# Revit family: P710076-031
name_source: partatom
category: Lighting Fixtures
revit_build: Autodesk Revit 2014 (Build: 20130308_1515(x64)
units: mm (PartAtom-declared; Revit-internal decimal feet)

## types (1)
- P710076-031
    Apparent Load = 60 VA
    Assembly Code = D5020200
    Color Filter = 16777215
    Connector Description = Lighting Connector
    Default Elevation = 48 "
    Description = Experience the sense of shelter, warmth, and protection offered by the mountain modern glow of this wall sconce. Let wandering eyes hungry for a satisfying lighting experience satiate their appetites as their gaze feasts upon the artistic yet playful tic-tac-toe pattern intricately weaved into the matte black frame. A signature seeded glass pane fosters a gazing window design that grants the light fixture a rustic, modern cabin vibe.
    Dimming Lamp Color Temperature Shift = <None>
    Fabric = Paint - Hubbell - White Texture
    Features = A signature seeded glass pane fosters a gazing window design that grants the light fixture a rustic, modern cabin vibe.
Let wandering eyes hungry for a satisfying lighting experience satiate their appetites as their gaze feasts upon the artistic yet playful tic-tac-toe pattern intricately weaved into the matte black frame.
Experience the sense of shelter, warmth, and protection offered by the mountain modern glow of this wall sconce.
Ideal for any foyer, dining room, or kitchen.
Measures 5-1/8-inch width by 14-5/8-inch height.
Uses one candelabra base bulb that is sold separately (60w max - LED or incandescent).
Able to be fully dimmable with dimmable bulbs.
Includes installation instructions and mounting hardware.
Progress Lighting products are designed for exceptional quality, reliability, and functionality.
    Fixture distribution = Direct
    Glass = Paint - Hubbell - White Texture
    Gold = Hubbell - Gold
    Height = 14.63 "
    Housing Material = Paint - Hubbell - Textured Camera Black
    Lamp = LED or Incandescent
    Load Classification = Lighting
    Manufacturer = Progress Lighting
    Model = P710076-031
    Photometric Web File = generic.ies
    Power Factor = 1
    Product Documentation Link = https://hubbellcdn.com
    Product Link = https://www.hubbell.com
    Tilt Angle = -90.00°
    URL = https://www.hubbell.com
    Voltage = 120 V
    Warranty = 5 years Warranty
    Wattage Comments = 60W
    Watts = 60 W
    Width = 5.13 "
    Wood = Wood Planks

## geometry (parser evidence)
native form markers: Sweep x4
no freeform markers — native parametric forms only
